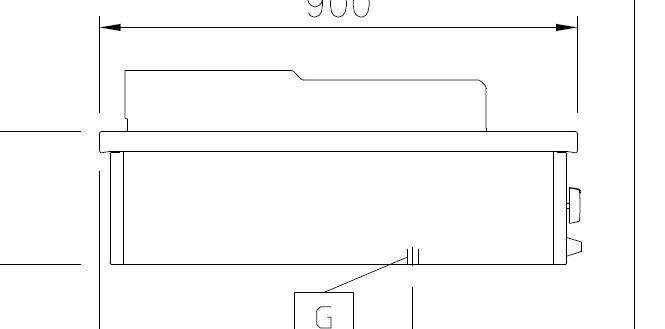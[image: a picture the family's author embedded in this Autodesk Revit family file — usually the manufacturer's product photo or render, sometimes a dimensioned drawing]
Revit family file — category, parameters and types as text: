
# Revit family: QF_ELECTROLUXPROFESSIONAL_589280_MCDBAAHOPO
name_source: partatom
category: Specialty Equipment
revit_build: Autodesk Revit 2018 (Build: 20190510_1515(x64)
units: mm (PartAtom-declared; Revit-internal decimal feet)

## family parameters
Always vertical = Yes
Cut with Voids When Loaded = No
Part Type = Normal
Room Calculation Point = No
Round Connector Dimension = Use Diameter
Shared = No
Work Plane-Based = No

## types (1)
- QF_ELECTROLUXPROFESSIONAL_589280_MCDBAAHOPO
    Description = GAS CHARGRILL,1-SIDE,800X900X250H
    Direct Waste Size = 0"
    Gas Connection Height = 0 mm  [stored 0 ft]
    Gas KW = 21
    Gas Size = 1"
    HP = 0 HP
    Manufacturer = ELECTROLUX
    Model = 589280
    Watts = 0 W
    Weight in Pounds = 253.5

note: [stored X ft] marks values corroborated as IEEE doubles in the binary element streams (Revit-internal decimal feet)

## geometry (parser evidence)
native form markers: Blend x27, Sweep x16
no freeform markers — native parametric forms only
